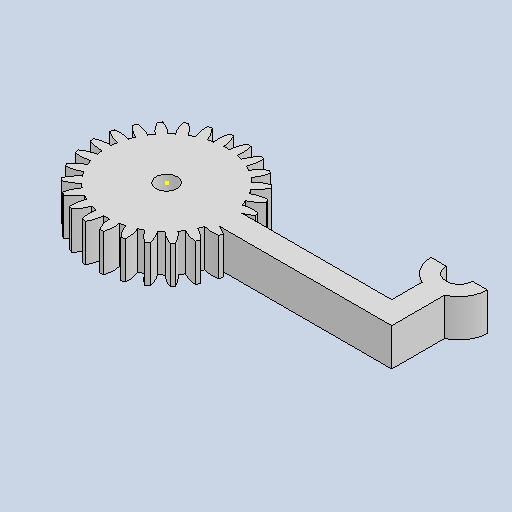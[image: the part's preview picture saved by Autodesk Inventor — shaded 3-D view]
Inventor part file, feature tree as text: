
AUTODESK INVENTOR PART (.ipt)
format: ipt  version: 2022 (Build 260153000, 153)  size: 358,400 bytes
history: native  units: in
note: dims shown in document units (in); Inventor stores cm internally (conversion verified against a paired STEP export)
features: sketch x13, extrude x12, pattern_circular x1
ambient origin geometry x8: Origin, YZ Plane, XZ Plane, XY Plane, X Axis, Y Axis, Z Axis, Center Point
bodies: Solid1 (feature_tree)
feature tree (26):
  extrude  "Extrusion1"  Depth=0.1575in
  pattern_circular  "Circular Pattern1"  Count=26 Angle=360.0deg
  extrude  "Extrusion6"  Depth=0.1969in
  extrude  "Extrusion7"  Depth=1.1811in
  extrude  "Extrusion8"  Depth=0.748in
  extrude  "Extrusion9"  Depth=0.1969in
  extrude  "Extrusion10"  Depth=0.1969in
  extrude  "Extrusion11"  Depth=0.1969in
  extrude  "Extrusion12"  Depth=0.1969in
  extrude  "Extrusion13"  Depth=0.1969in
  extrude  "Extrusion14"  Depth=0.1969in
  extrude  "Extrusion15"  Depth=0.1181in
  sketch  "Sketch18"  dims[d56=0.748in d57=0.1969in]
  extrude  "Extrusion16"  Depth=0.1969in
  sketch  "Sketch1"  dims[d0=0.6299in d1=0.1575in]
  sketch  "Sketch8"  dims[d2=0.0098in]
  sketch  "Sketch9"  dims[d3=0.0098in]
  sketch  "Sketch10"  dims[d4=0.0236in]
  sketch  "Sketch11"  dims[d7=0.0472in]
  sketch  "Sketch12"  dims[d8=0.1772in]
  sketch  "Sketch13"  dims[d10=0.0787in]
  sketch  "Sketch14"  dims[d11=0.1969in d12=0.0in d13=10.2362in d14=360.0deg]
  sketch  "Sketch15"  dims[d49=0.1969in d50=0.1575in]
  sketch  "Sketch16"  dims[d51=0.5438in d52=0.0in d53=1.1811in]
  sketch  "Sketch17"  dims[d54=0.7087in d55=0.748in]
  sketch  "Sketch19"  dims[d58=0.9843in d59=0.0591in d60=0.0591in d61=0.0591in d62=0.3543in d63=0.0591in d64=0.1181in d65=0.1969in d66=0.0197in d67=0.0197in d68=0.0197in d69=0.1969in d70=0.0in d71=1.1811in d72=0.3543in d73=0.1181in d74=0.1181in d75=0.3543in d76=0.1181in d77=0.1969in d78=0.0197in d79=0.1969in d80=0.0197in d81=0.0197in d82=0.1969in d83=0.0in d84=0.1811in d85=0.1969in d86=0.0in d87=1.1811in d88=0.3543in d89=0.1378in d90=0.3937in d91=0.0in d92=0.3937in d93=0.0in d94=1.1811in d95=0.3543in d96=0.1181in d97=0.1378in d98=0.1969in d99=0.1969in d100=0.0in d101=0.1969in d102=0.0in d103=0.1102in d104=0.1969in d105=0.0in d106=0.2874in d107=0.1181in d108=0.0in d109=0.2953in d110=0.1969in d111=0.0in]
